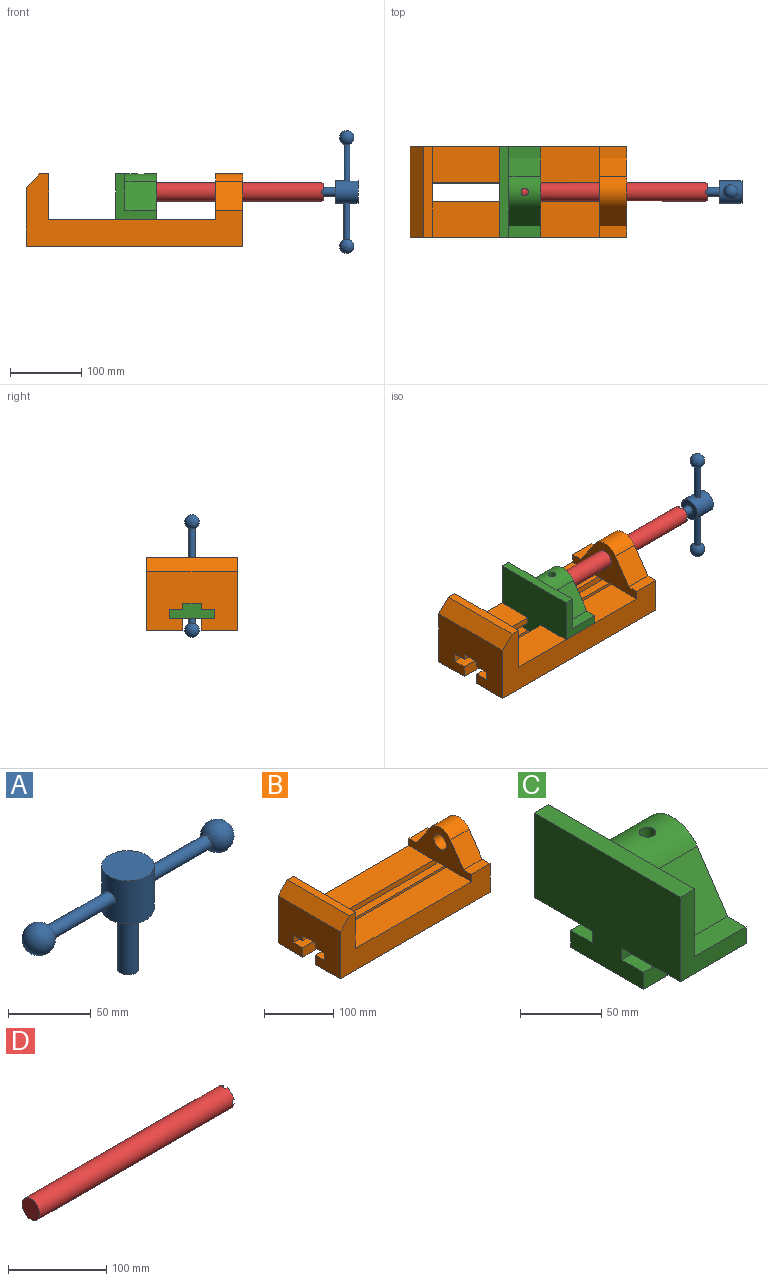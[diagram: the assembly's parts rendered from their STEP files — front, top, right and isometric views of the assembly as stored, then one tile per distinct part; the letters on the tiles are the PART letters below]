
ASSEMBLY  parts=4 mates=3
PART A: 13 faces, bbox 172.7x31.8x76.2 mm
  f0: cylinder r=15.88mm len=31.75mm, axis (0,0,-1), area 3041.4mm2, adj f1,f2,f5,f6
  f1: plane 31.75x31.75mm, normal (0,0,1), area 791.7mm2, adj f0
  f2: plane 31.75x31.75mm, normal (0,0,-1), area 665.1mm2, adj f0,f3
  f3: cylinder r=6.35mm len=44.45mm, axis (0,0,-1), area 1773.5mm2, adj f2,f4
  f4: plane 12.7x12.7mm, normal (0,0,-1), area 126.7mm2, adj f3
  f5: cylinder r=4.45mm len=51.82mm, axis (-1,0,0), area 1438.5mm2, adj f0,f7
  f6: cylinder r=4.45mm len=51.82mm, axis (-1,0,0), area 1438.5mm2, adj f0,f8
  f7: sphere r=10.16mm, area 1231.8mm2, adj f5
  f8: sphere r=10.16mm, area 1231.8mm2, adj f6
  f9: sphere r=4.45mm, area 124.1mm2, adj f10
  f10: plane 8.89x8.89mm, normal (1,0,0), area 62.1mm2, adj f9
  f11: sphere r=4.45mm, area 124.1mm2, adj f12
  f12: plane 8.89x8.89mm, normal (-1,0,0), area 62.1mm2, adj f11
PART B: 30 faces, bbox 304.8x127x101.6 mm
  f0: plane 38.1x25.4mm, normal (0,0,-1), area 967.7mm2, adj f17,f19,f23,f27
  f1: plane 127x12.7mm, normal (0,0,1), area 1612.9mm2, adj f2,f3,f25,f26
  f2: plane 304.8x101.6mm, normal (0,1,0), area 13931.4mm2, adj f1,f6,f7,f23,f24,f25,f26,f27
  f3: plane 304.8x101.6mm, normal (0,-1,0), area 13931.4mm2, adj f1,f11,f12,f23,f24,f25,f26,f27
  f4: plane 304.8x19.05mm, normal (0,0,1), area 5806.4mm2, adj f5,f22,f23,f24
  f5: plane 304.8x16.51mm, normal (0,-1,0), area 5032.2mm2, adj f4,f6,f23,f24
  f6: plane 304.8x50.8mm, normal (0,0,-1), area 15483.8mm2, adj f2,f5,f23,f24
  f7: plane 38.1x15.88mm, normal (0,0,1), area 604.8mm2, adj f2,f8,f23,f27
  f8: plane 39.55x38.1mm, normal (0,0.83,0.56), area 1814.5mm2, adj f7,f9,f23,f27
  f9: cylinder r=25.4mm len=42.19mm, axis (-1,0,0), area 1896.6mm2, adj f8,f10,f23,f27
  f10: plane 39.55x38.1mm, normal (0,-0.83,0.56), area 1814.5mm2, adj f9,f11,f23,f27
  f11: plane 38.1x15.88mm, normal (0,0,1), area 604.8mm2, adj f3,f10,f23,f27
  f12: plane 304.8x50.8mm, normal (0,0,-1), area 15483.8mm2, adj f3,f13,f23,f24
  f13: plane 304.8x16.51mm, normal (0,1,0), area 5032.2mm2, adj f12,f14,f23,f24
  f14: plane 304.8x19.05mm, normal (0,0,1), area 5806.4mm2, adj f13,f15,f23,f24
  f15: plane 304.8x12.7mm, normal (0,1,0), area 3871mm2, adj f14,f16,f23,f24
  f16: plane 304.8x19.05mm, normal (0,0,-1), area 5806.4mm2, adj f15,f17,f23,f24
  f17: plane 304.8x8.89mm, normal (0,1,0), area 2709.7mm2, adj f0,f16,f18,f23,f24,f29
  f18: plane 31.75x25.4mm, normal (0,0,-1), area 806.4mm2, adj f17,f19,f24,f26
  f19: plane 304.8x8.89mm, normal (0,-1,0), area 2709.7mm2, adj f0,f18,f20,f23,f24,f28
  f20: plane 304.8x19.05mm, normal (0,0,-1), area 5806.4mm2, adj f19,f22,f23,f24
  f21: cylinder r=12.7mm len=38.1mm, axis (-1,0,0), area 3040.2mm2, adj f23,f27
  f22: plane 304.8x12.7mm, normal (0,-1,0), area 3871mm2, adj f4,f20,f23,f24
  f23: plane 127x101.6mm, normal (1,0,0), area 7544.8mm2, adj f0,f2,f3,f4,f5,f6,f7,f8
  f24: plane 127x82.55mm, normal (-1,0,0), area 9032.2mm2, adj f2,f3,f4,f5,f6,f12,f13,f14
  f25: plane 127x19.05mm, normal (-0.71,0,0.71), area 3421.5mm2, adj f1,f2,f3,f24
  f26: plane 127x63.5mm, normal (1,0,0), area 8064.5mm2, adj f1,f2,f3,f18,f28,f29
  f27: plane 127x63.5mm, normal (-1,0,0), area 4157.7mm2, adj f0,f2,f3,f7,f8,f9,f10,f11
  f28: plane 234.95x50.8mm, normal (0,0,1), area 11935.5mm2, adj f2,f19,f26,f27
  f29: plane 234.95x50.8mm, normal (0,0,1), area 11935.5mm2, adj f3,f17,f26,f27
PART C: 24 faces, bbox 57.2x127x85.1 mm
  f0: cylinder r=12.7mm len=44.45mm, axis (-1,0,0), area 3464.4mm2, adj f17,f22,f23
  f1: plane 63.5x57.15mm, normal (0,1,0), area 1371mm2, adj f2,f16,f17,f19,f20,f21
  f2: plane 44.45x15.88mm, normal (0,0,1), area 705.6mm2, adj f1,f3,f17,f21
  f3: plane 44.45x39.55mm, normal (0,0.83,0.56), area 2116.9mm2, adj f2,f4,f17,f21
  f4: cylinder r=25.4mm len=44.45mm, axis (-1,0,0), area 2131.3mm2, adj f3,f5,f17,f18,f21,f23
  f5: plane 44.45x39.55mm, normal (0,-0.83,0.56), area 2116.9mm2, adj f4,f6,f17,f18
  f6: plane 44.45x15.88mm, normal (0,0,1), area 705.6mm2, adj f5,f7,f17,f18
  f7: plane 63.5x57.15mm, normal (0,-1,0), area 1371mm2, adj f6,f8,f17,f18,f19,f20
  f8: plane 57.15x50.8mm, normal (0,0,-1), area 2903.2mm2, adj f7,f9,f17,f19
  f9: plane 57.15x8.89mm, normal (0,-1,0), area 508.1mm2, adj f8,f10,f17,f19
  f10: plane 57.15x19.05mm, normal (0,0,1), area 1088.7mm2, adj f9,f11,f17,f19
  f11: plane 57.15x12.7mm, normal (0,-1,0), area 725.8mm2, adj f10,f12,f17,f19
  f12: plane 63.5x57.15mm, normal (0,0,-1), area 3629mm2, adj f11,f13,f17,f19
  f13: plane 57.15x12.7mm, normal (0,1,0), area 725.8mm2, adj f12,f14,f17,f19
  f14: plane 57.15x19.05mm, normal (0,0,1), area 1088.7mm2, adj f13,f15,f17,f19
  f15: plane 57.15x8.89mm, normal (0,1,0), area 508.1mm2, adj f14,f16,f17,f19
  f16: plane 57.15x50.8mm, normal (0,0,-1), area 2903.2mm2, adj f1,f15,f17,f19
  f17: plane 127x85.09mm, normal (1,0,0), area 5190mm2, adj f0,f1,f2,f3,f4,f5,f6,f7
  f18: plane 63.5x50.8mm, normal (1,0,0), area 1700mm2, adj f4,f5,f6,f7,f20
  f19: plane 127x85.09mm, normal (-1,0,0), area 9096.8mm2, adj f1,f7,f8,f9,f10,f11,f12,f13
  f20: plane 127x12.7mm, normal (0,0,1), area 1612.9mm2, adj f1,f7,f18,f19,f21
  f21: plane 63.5x50.8mm, normal (1,0,0), area 1700mm2, adj f1,f2,f3,f4,f20
  f22: plane 25.4x25.4mm, normal (1,0,0), area 506.7mm2, adj f0
  f23: cylinder r=5.08mm len=13.76mm, axis (0,0,1), area 413.9mm2, adj f0,f4
PART D: 20 faces, bbox 279.4x25.4x25.4 mm
  f0: plane 6.88x5.08mm, normal (1,0,0), area 32.7mm2, adj f4,f6,f8,f11
  f1: plane 6.88x5.08mm, normal (1,0,0), area 32.7mm2, adj f4,f6,f10,f13
  f2: plane 6.88x5.08mm, normal (1,0,0), area 32.7mm2, adj f4,f6,f14,f16
  f3: plane 6.88x5.08mm, normal (1,0,0), area 32.7mm2, adj f4,f6,f7,f17
  f4: cylinder r=12.7mm len=279.4mm, axis (-1,0,0), area 22243.2mm2, adj f0,f1,f2,f3,f5,f7,f8,f9
  f5: plane 25.4x25.4mm, normal (-1,0,0), area 506.7mm2, adj f4
  f6: cylinder r=6.35mm len=27.94mm, axis (-1,0,0), area 1061.7mm2, adj f0,f1,f2,f3,f7,f8,f9,f10
  f7: plane 6.62x2.54mm, normal (0,0,-1), area 16.8mm2, adj f3,f4,f6,f9
  f8: plane 6.62x2.54mm, normal (0,-1,0), area 16.8mm2, adj f0,f4,f6,f9
  f9: plane 9.9x9.9mm, normal (1,0,0), area 62.3mm2, adj f4,f6,f7,f8
  f10: plane 6.62x2.54mm, normal (0,0,-1), area 16.8mm2, adj f1,f4,f6,f12
  f11: plane 6.62x2.54mm, normal (0,1,0), area 16.8mm2, adj f0,f4,f6,f12
  f12: plane 9.9x9.9mm, normal (1,0,0), area 62.3mm2, adj f4,f6,f10,f11
  f13: plane 6.62x2.54mm, normal (0,0,1), area 16.8mm2, adj f1,f4,f6,f15
  f14: plane 6.62x2.54mm, normal (0,1,0), area 16.8mm2, adj f2,f4,f6,f15
  f15: plane 9.9x9.9mm, normal (1,0,0), area 62.3mm2, adj f4,f6,f13,f14
  f16: plane 6.62x2.54mm, normal (0,-1,0), area 16.8mm2, adj f2,f4,f6,f18
  f17: plane 6.62x2.54mm, normal (0,0,1), area 16.8mm2, adj f3,f4,f6,f18
  f18: plane 9.9x9.9mm, normal (1,0,0), area 62.3mm2, adj f4,f6,f16,f17
  f19: plane 12.7x12.7mm, normal (1,0,0), area 126.7mm2, adj f6
PLACE A rot(axis=(0,1,0),90deg) t=(378.03,64.09,66.76)mm
PLACE B t=(209.77,0.59,-9.44)mm fixed
PLACE C t=(82.12,64.09,7.07)mm
PLACE D t=(82.12,64.09,66.76)mm
MATE revolute C.f0 <-> D.f4  axis (-1,0,0) through (82.12,64.09,66.76)mm
MATE fastened D.f4 <-> A.f0  axis (1,0,0) through (333.58,64.09,66.76)mm
MATE slider B.f26 <-> C.f17  axis (1,0,0) through (-25.18,0.59,28.66)mm
